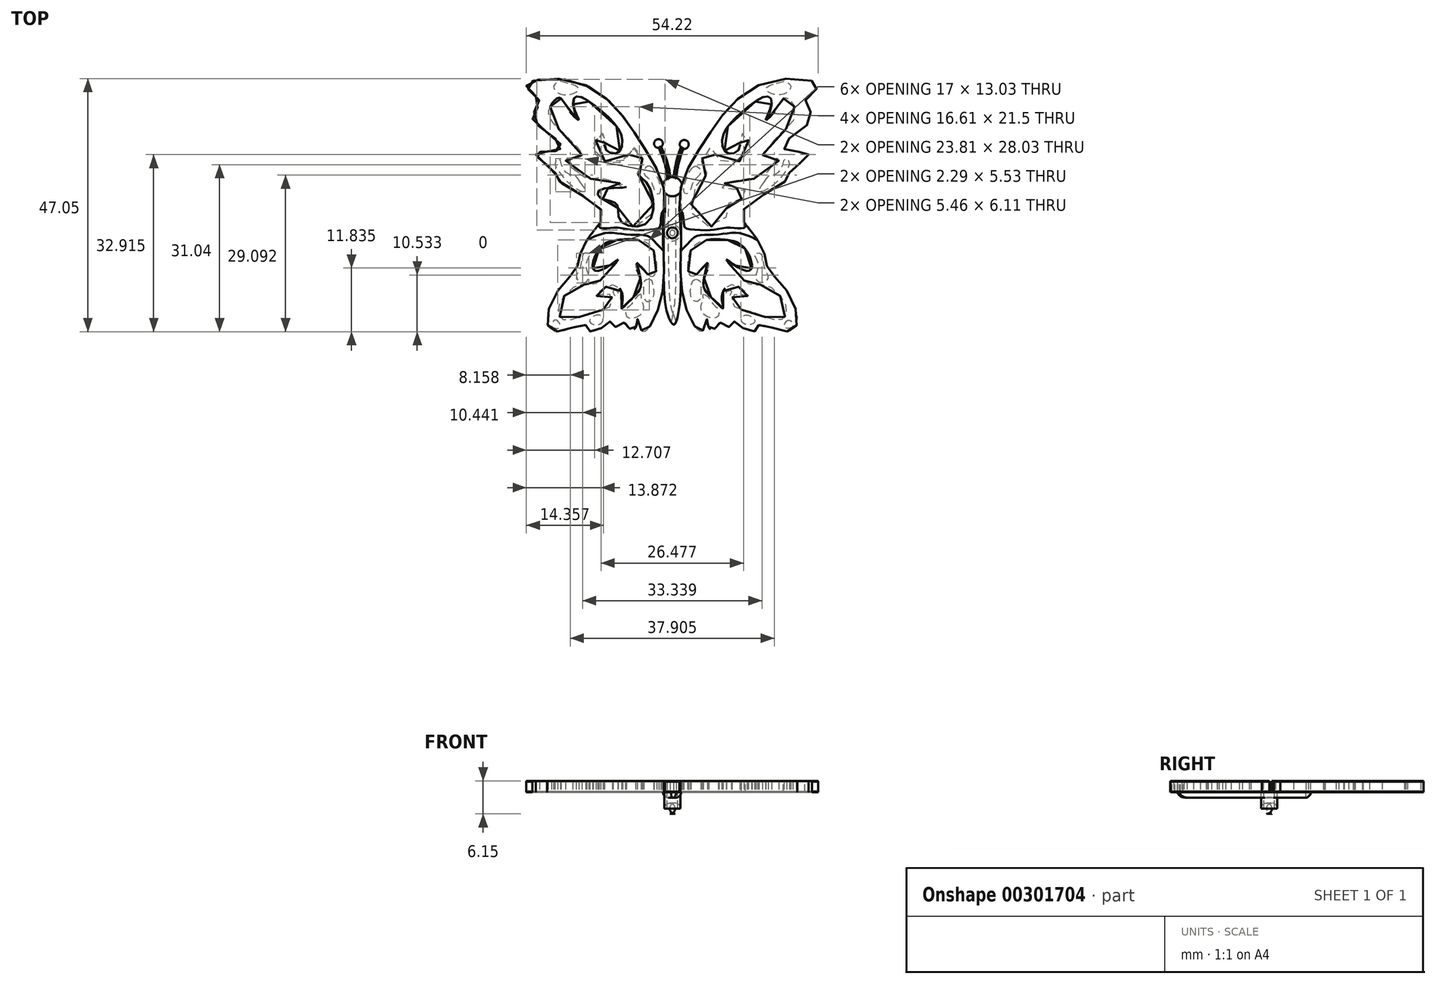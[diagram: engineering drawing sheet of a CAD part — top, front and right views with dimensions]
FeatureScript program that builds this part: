
annotation { "Feature Type Name" : "Feature", "Feature Type Description" : "" }
export const myFeature = defineFeature(function(context is Context, id is Id, definition is map)
    precondition{}
    {
        {
            var Q0;
            Q0=qCreatedBy(makeId("Top.planeOp"),FACE);
            var sketch = newSketch(context, id + "F0", { "sketchPlane" : qUnion([Q0])});
            skFitSpline(sketch, "E0", {"points": [v(3.62, 15.78) * mm, v(8.1, 22.3) * mm, v(17.17, 28.33) * mm, v(25.51, 27.33) * mm, v(23.06, 24.4) * mm, v(24.4, 21.43) * mm, v(19.29, 16.73) * mm, v(19.62, 15.33) * mm, v(23.6, 14.88) * mm, v(23.2, 13.8) * mm, v(20.17, 11.2) * mm, v(19.8, 10) * mm, v(11.56, 4.2) * mm, v(12.4, 1.11) * mm, v(15.39, -3.48) * mm, v(16.15, -6.56) * mm, v(19.7, -10.78) * mm, v(21.48, -17.24) * mm, v(18.78, -18.22) * mm, v(14.52, -17.12) * mm, v(13.9, -18.22) * mm, v(11.37, -17.59) * mm, v(9.8, -16.49) * mm, v(8.84, -17.52) * mm, v(7.16, -16.68) * mm, v(6.11, -18) * mm, v(5.16, -17.53) * mm, v(4.84, -16.03) * mm, v(4.01, -18.26) * mm, v(1.8, -16.04) * mm, v(0, -8.85) * mm, v(0, 0) * mm, v(0, 8.4) * mm, v(3.62, 15.78) * mm]});
            skFitSpline(sketch, "E1", {"points": [v(21.1, 23.42) * mm, v(21.2, 21.34) * mm, v(15.67, 15.5) * mm, v(15.5, 14) * mm, v(18.2, 13.66) * mm, v(14, 10.1) * mm, v(12.49, 10.25) * mm, v(6.95, 8.53) * mm, v(11.74, 8.05) * mm, v(12.11, 6.85) * mm, v(10.13, 5.96) * mm, v(8.56, 5.14) * mm, v(8.1, 2.24) * mm, v(2.94, 1.96) * mm, v(2.94, 8.98) * mm, v(4.9, 11.2) * mm, v(3.88, 13) * mm, v(5.47, 15.82) * mm, v(7.16, 13.57) * mm, v(11.21, 13.42) * mm, v(13.05, 16.2) * mm, v(11.08, 18.59) * mm, v(10.9, 15.8) * mm, v(8.56, 14.88) * mm, v(7.72, 17.69) * mm, v(10.9, 22.09) * mm, v(16.14, 25.37) * mm, v(16.8, 23.68) * mm, v(15.77, 20.97) * mm, v(17.69, 22.94) * mm, v(19.23, 25.09) * mm, v(20.17, 24.71) * mm, v(21.1, 23.42) * mm]});
            skFitSpline(sketch, "E2", {"points": [v(4.72, -1.32) * mm, v(8.84, -1.32) * mm, v(11.84, -2.82) * mm, v(13.16, -6.56) * mm, v(11.65, -6.94) * mm, v(8.47, -4.97) * mm, v(10.25, -7.22) * mm, v(13.16, -9.65) * mm, v(15.96, -9.75) * mm, v(19.62, -14.05) * mm, v(18.4, -16.2) * mm, v(13.16, -14.71) * mm, v(9.78, -13.5) * mm, v(10.06, -11.43) * mm, v(12.5, -11.71) * mm, v(12.12, -11.06) * mm, v(9.4, -9.65) * mm, v(7.62, -11.62) * mm, v(7.81, -14.06) * mm, v(6.31, -12.65) * mm, v(4.16, -9.47) * mm, v(5.19, -5.81) * mm, v(4.72, -5.63) * mm, v(3.03, -7.6) * mm, v(2, -8.06) * mm, v(1.35, -6.94) * mm, v(2, -3) * mm, v(4.72, -1.32) * mm]});
            skFitSpline(sketch, "E3", {"points": [v(17.73, 27.77) * mm, v(18.86, 28.09) * mm, v(19.76, 28.01) * mm, v(20.43, 27.23) * mm, v(19.87, 26.2) * mm, v(17.97, 25.65) * mm, v(16.23, 26.2) * mm, v(15.76, 26.8) * mm, v(16.86, 27.53) * mm, v(17.73, 27.77) * mm]});
            skFitSpline(sketch, "E4", {"points": [v(15.48, 9.43) * mm, v(16.48, 10.66) * mm, v(17.68, 10.96) * mm, v(18.85, 12.36) * mm, v(19.4, 13.8) * mm, v(20.17, 13.05) * mm, v(19.43, 11.38) * mm, v(18.32, 9.96) * mm, v(15.76, 7.93) * mm, v(14.5, 7.76) * mm, v(15.48, 9.43) * mm]});
            skFitSpline(sketch, "E5", {"points": [v(2.27, 12.22) * mm, v(2.94, 12.38) * mm, v(3.73, 11.27) * mm, v(2.43, 9.7) * mm, v(1.52, 7.5) * mm, v(0.81, 7.3) * mm, v(0.54, 8.36) * mm, v(1.52, 11.2) * mm, v(2.27, 12.22) * mm]});
            skFitSpline(sketch, "E6", {"points": [v(14.05, -3.77) * mm, v(14.84, -3.84) * mm, v(15.26, -5.17) * mm, v(15.7, -7.06) * mm, v(16.23, -8.1) * mm, v(15.6, -9.11) * mm, v(14.48, -9.18) * mm, v(13.93, -8.16) * mm, v(14.22, -7.04) * mm, v(14.4, -6.12) * mm, v(14.1, -4.92) * mm, v(13.7, -3.96) * mm, v(14.05, -3.77) * mm]});
            skFitSpline(sketch, "E7", {"points": [v(8.84, -10.78) * mm, v(9.35, -10.78) * mm, v(9.24, -11.43) * mm, v(8.84, -11.63) * mm, v(8.44, -11.12) * mm, v(8.84, -10.78) * mm]});
            skFitSpline(sketch, "E8", {"points": [v(2.43, -8.72) * mm, v(3.47, -8.85) * mm, v(3.73, -10) * mm, v(3.73, -11.43) * mm, v(3.31, -12.65) * mm, v(2.43, -12.65) * mm, v(1.8, -11.43) * mm, v(2, -9.47) * mm, v(2.43, -8.72) * mm]});
            skFitSpline(sketch, "E9", {"points": [v(4.16, -11.43) * mm, v(4.94, -11.82) * mm, v(6, -13.29) * mm, v(6.94, -14.25) * mm, v(6.9, -15.53) * mm, v(5.77, -15.85) * mm, v(4.16, -15.07) * mm, v(3.73, -13.53) * mm, v(4.16, -12.27) * mm, v(4.16, -11.43) * mm]});
            skFitSpline(sketch, "E10", {"points": [v(11.65, -15.43) * mm, v(13.07, -15.53) * mm, v(13.74, -16.49) * mm, v(12.7, -17.08) * mm, v(11.3, -16.49) * mm, v(11.65, -15.43) * mm]});
            skFitSpline(sketch, "E11", {"points": [v(19.4, -16.73) * mm, v(20.17, -16.23) * mm, v(20.82, -17.24) * mm, v(20.17, -17.72) * mm, v(19.23, -17.53) * mm, v(19.4, -16.73) * mm]});
            skFitSpline(sketch, "E12", {"points": [v(14.26, -1.36) * mm, v(12.63, -0.57) * mm, v(10.17, 0) * mm, v(6.28, -0.33) * mm, v(2.9, -0.61) * mm, v(1.57, -1.74) * mm, v(0, -3.4) * mm], "startDerivative": vector(-10.7, 6.1) * mm, "endDerivative": vector(-9.7, -12.04) * mm});
            skFitSpline(sketch, "E13", {"points": [v(11.7, 2.04) * mm, v(12, 1.28) * mm, v(11.81, 0.96) * mm, v(10.6, 0.84) * mm, v(9, 0.99) * mm, v(6.88, 0.7) * mm, v(4.9, 0.47) * mm, v(1.68, 0.66) * mm, v(0.68, 1.09) * mm, v(0.42, 3.4) * mm, v(-0.27, 4.56) * mm], "startDerivative": vector(6.08, -11.32) * mm, "endDerivative": vector(-8.37, 10.05) * mm});
            skSolve(sketch);
        }
        {
            var Q0;
            Q0=qCreatedBy(makeId("Top.planeOp"),FACE);
            var sketch = newSketch(context, id + "F1", { "sketchPlane" : qUnion([Q0])});
            skCircle(sketch, "E14", {"center": v(0.63, 16.43) * mm, "radius": 0.84 * mm});
            skCircle(sketch, "E15", {"center": v(-1.57, 8.6) * mm, "radius": 1.8 * mm});
            skFitSpline(sketch, "E16", {"points": [v(-1.33, 10.38) * mm, v(0, 15.89) * mm], "startDerivative": vector(0.59, 5.64) * mm, "endDerivative": vector(2.02, 4.96) * mm});
            skFitSpline(sketch, "E17", {"points": [v(-0.83, 10.24) * mm, v(0.45, 15.62) * mm], "startDerivative": vector(0.54, 5.8) * mm, "endDerivative": vector(2.53, 6.6) * mm});
            skCircle(sketch, "E18", {"center": v(-4.16, 16.6) * mm, "radius": 0.81 * mm});
            skFitSpline(sketch, "E19", {"points": [v(-3.65, 15.97) * mm, v(-2.01, 10.34) * mm], "startDerivative": vector(2.88, -5.93) * mm, "endDerivative": vector(0.23, -5.97) * mm});
            skFitSpline(sketch, "E20", {"points": [v(-4.1, 15.8) * mm, v(-2.54, 10.1) * mm], "startDerivative": vector(2.85, -7.12) * mm, "endDerivative": vector(0.3, -6.34) * mm});
            skFitSpline(sketch, "E21", {"points": [v(0, 7.7) * mm, v(0.03, 0) * mm, v(0, -9.31) * mm, v(-0.4, -14.6) * mm, v(-1.33, -17.08) * mm, v(-2.61, -14.6) * mm, v(-3.15, -9.6) * mm, v(-3.3, 0) * mm, v(-3.17, 7.78) * mm], "startDerivative": vector(0.94, -63.78) * mm, "endDerivative": vector(1.9, 50.03) * mm});
            skCircle(sketch, "E22", {"center": v(-1.57, 0) * mm, "radius": 1 * mm});
            skCircle(sketch, "E23", {"center": v(-1.57, 0) * mm, "radius": 1.5 * mm});
            skSolve(sketch);
        }
        {
            var Q0;
            Q0=qCreatedBy(makeId("Right.planeOp"),FACE);
            cPlane(context, id + "F2", {"entities" : qUnion([Q0]), "cplaneType" : CPlaneType.OFFSET, "offset" : 1.6 * mm, "oppositeDirection" : true, "width" : 150 * mm, "height" : 150 * mm});
        }
        {
            var Q0;
            Q0=makeQuery(id+"F0.imprint","IMPRINT",FACE,{"disambiguationData":[TD([[makeQuery(id+"F0.imprint","IMPRINT",EDGE,{"derivedFrom":sQuery(id+"F0.wireOp",EDGE,"E1")}),1.0]])]});
            var Q1;
            {var subQ0=sQuery(id+"F0.wireOp",EDGE,"E12");Q1=makeQuery(id+"F0.imprint","IMPRINT",FACE,{"disambiguationData":[TD([[makeQuery(id+"F0.imprint","IMPRINT",EDGE,{"derivedFrom":subQ0}),-1.0]])]});}
            var Q2;
            Q2=makeQuery(id+"F0.imprint","IMPRINT",FACE,{"disambiguationData":[TD([[makeQuery(id+"F0.imprint","IMPRINT",EDGE,{"derivedFrom":sQuery(id+"F0.wireOp",EDGE,"E2")}),1.0]])]});
            var Q3;
            Q3=makeQuery(id+"F0.imprint","IMPRINT",FACE,{"disambiguationData":[TD([[makeQuery(id+"F0.imprint","IMPRINT",EDGE,{"derivedFrom":sQuery(id+"F0.wireOp",EDGE,"E8")}),-1.0]])]});
            var Q4;
            Q4=makeQuery(id+"F0.imprint","IMPRINT",FACE,{"disambiguationData":[TD([[makeQuery(id+"F0.imprint","IMPRINT",EDGE,{"derivedFrom":sQuery(id+"F0.wireOp",EDGE,"E9")}),-1.0]])]});
            var Q5;
            Q5=makeQuery(id+"F0.imprint","IMPRINT",FACE,{"disambiguationData":[TD([[makeQuery(id+"F0.imprint","IMPRINT",EDGE,{"derivedFrom":sQuery(id+"F0.wireOp",EDGE,"E7")}),-1.0]])]});
            var Q6;
            Q6=makeQuery(id+"F0.imprint","IMPRINT",FACE,{"disambiguationData":[TD([[makeQuery(id+"F0.imprint","IMPRINT",EDGE,{"derivedFrom":sQuery(id+"F0.wireOp",EDGE,"E10")}),-1.0]])]});
            var Q7;
            Q7=makeQuery(id+"F0.imprint","IMPRINT",FACE,{"disambiguationData":[TD([[makeQuery(id+"F0.imprint","IMPRINT",EDGE,{"derivedFrom":sQuery(id+"F0.wireOp",EDGE,"E6")}),-1.0]])]});
            var Q8;
            Q8=makeQuery(id+"F0.imprint","IMPRINT",FACE,{"disambiguationData":[TD([[makeQuery(id+"F0.imprint","IMPRINT",EDGE,{"derivedFrom":sQuery(id+"F0.wireOp",EDGE,"E4")}),-1.0]])]});
            var Q9;
            Q9=makeQuery(id+"F0.imprint","IMPRINT",FACE,{"disambiguationData":[TD([[makeQuery(id+"F0.imprint","IMPRINT",EDGE,{"derivedFrom":sQuery(id+"F0.wireOp",EDGE,"E3")}),-1.0]])]});
            var Q10;
            Q10=makeQuery(id+"F0.imprint","IMPRINT",FACE,{"disambiguationData":[TD([[makeQuery(id+"F0.imprint","IMPRINT",EDGE,{"derivedFrom":sQuery(id+"F0.wireOp",EDGE,"E5")}),-1.0]])]});
            var Q11;
            Q11=makeQuery(id+"F0.imprint","IMPRINT",FACE,{"disambiguationData":[TD([[makeQuery(id+"F0.imprint","IMPRINT",EDGE,{"derivedFrom":sQuery(id+"F0.wireOp",EDGE,"E11")}),-1.0]])]});
            extrude(context, id + "F3", {"entities" : qUnion([Q0, Q1, Q2, Q3, Q4, Q5, Q6, Q7, Q8, Q9, Q10, Q11]), "depth" : 0.15 * mm});
        }
        {
            var Q0;
            Q0=makeQuery(id+"F0.imprint","IMPRINT",FACE,{"disambiguationData":[TD([[makeQuery(id+"F0.imprint","IMPRINT",EDGE,{"derivedFrom":sQuery(id+"F0.wireOp",EDGE,"E1")}),1.0]])]});
            var Q1;
            Q1=makeQuery(id+"F0.imprint","IMPRINT",FACE,{"disambiguationData":[TD([[makeQuery(id+"F0.imprint","IMPRINT",EDGE,{"derivedFrom":sQuery(id+"F0.wireOp",EDGE,"E2")}),1.0]])]});
            extrude(context, id + "F4", {"entities" : qUnion([Q0, Q1]), "depth" : 2 * mm});
        }
        {
            var Q0;
            Q0=makeQuery(id+"F3.opExtrude","SWEPT_BODY",BODY,{"disambiguationData":[OSD([sQuery(id+"F0.wireOp",EDGE,"E0"),sQuery(id+"F0.wireOp",EDGE,"E1"),sQuery(id+"F0.wireOp",EDGE,"E2")])]});
            transform(context, id + "F5", {"entities" : qUnion([Q0]), "transformType" : TransformType.TRANSLATION_3D, "dx" : 0 * mm, "dy" : 0 * mm, "dz" : 2 * mm, "makeCopy" : true});
        }
        {
            var Q0;
            {var subQ0=sQuery(id+"F0.wireOp",EDGE,"E12");Q0=makeQuery(id+"F0.imprint","IMPRINT",FACE,{"disambiguationData":[TD([[makeQuery(id+"F0.imprint","IMPRINT",EDGE,{"derivedFrom":subQ0}),-1.0]])]});}
            extrude(context, id + "F6", {"entities" : qUnion([Q0]), "depth" : 25 * mm});
        }
        {
            var Q0;
            Q0=makeQuery(id+"F6.opExtrude","SWEPT_BODY",BODY,{"disambiguationData":[OSD([sQuery(id+"F0.wireOp",EDGE,"E0"),sQuery(id+"F0.wireOp",EDGE,"E12"),sQuery(id+"F0.wireOp",EDGE,"E13")])]});
            var Q1;
            Q1=makeQuery(id+"F5.opPattern","COPY",BODY,{"derivedFrom":makeQuery(id+"F3.opExtrude","SWEPT_BODY",BODY,{"disambiguationData":[OSD([sQuery(id+"F0.wireOp",EDGE,"E0"),sQuery(id+"F0.wireOp",EDGE,"E1"),sQuery(id+"F0.wireOp",EDGE,"E2")])]}),"instanceName":"1"});
            booleanBodies(context, id + "F7", {"operationType" : BooleanOperationType.SUBTRACTION, "tools" : qUnion([Q0]), "targets" : qUnion([Q1])});
        }
        {
            var Q0;
            Q0=makeQuery(id+"F3.opExtrude","SWEPT_BODY",BODY,{"disambiguationData":[OSD([sQuery(id+"F0.wireOp",EDGE,"E0"),sQuery(id+"F0.wireOp",EDGE,"E1"),sQuery(id+"F0.wireOp",EDGE,"E2")])]});
            var Q1;
            Q1=makeQuery(id+"F4.opExtrude","SWEPT_BODY",BODY,{"disambiguationData":[OSD([sQuery(id+"F0.wireOp",EDGE,"E0"),sQuery(id+"F0.wireOp",EDGE,"E2"),sQuery(id+"F0.wireOp",EDGE,"E6"),sQuery(id+"F0.wireOp",EDGE,"E7"),sQuery(id+"F0.wireOp",EDGE,"E8"),sQuery(id+"F0.wireOp",EDGE,"E9"),sQuery(id+"F0.wireOp",EDGE,"E10"),sQuery(id+"F0.wireOp",EDGE,"E11"),sQuery(id+"F0.wireOp",EDGE,"E12")])]});
            var Q2;
            Q2=makeQuery(id+"F4.opExtrude","SWEPT_BODY",BODY,{"disambiguationData":[OSD([sQuery(id+"F0.wireOp",EDGE,"E0"),sQuery(id+"F0.wireOp",EDGE,"E1"),sQuery(id+"F0.wireOp",EDGE,"E3"),sQuery(id+"F0.wireOp",EDGE,"E4"),sQuery(id+"F0.wireOp",EDGE,"E5"),sQuery(id+"F0.wireOp",EDGE,"E13")])]});
            var Q3;
            Q3=makeQuery(id+"F7.opBoolean","SPLIT",BODY,{"disambiguationData":[OD(0.0)],"derivedFrom":makeQuery(id+"F5.opPattern","COPY",BODY,{"derivedFrom":makeQuery(id+"F3.opExtrude","SWEPT_BODY",BODY,{"disambiguationData":[OSD([sQuery(id+"F0.wireOp",EDGE,"E0"),sQuery(id+"F0.wireOp",EDGE,"E1"),sQuery(id+"F0.wireOp",EDGE,"E2")])]}),"instanceName":"1"})});
            var Q4;
            Q4=makeQuery(id+"F7.opBoolean","SPLIT",BODY,{"disambiguationData":[OD(1.0)],"derivedFrom":makeQuery(id+"F5.opPattern","COPY",BODY,{"derivedFrom":makeQuery(id+"F3.opExtrude","SWEPT_BODY",BODY,{"disambiguationData":[OSD([sQuery(id+"F0.wireOp",EDGE,"E0"),sQuery(id+"F0.wireOp",EDGE,"E1"),sQuery(id+"F0.wireOp",EDGE,"E2")])]}),"instanceName":"1"})});
            var Q5;
            Q5=qCreatedBy(id+"F2.planeOp",FACE);
            mirror(context, id + "F8", {"entities" : qUnion([Q0, Q1, Q2, Q3, Q4]), "mirrorPlane" : qUnion([Q5])});
        }
        {
            var Q0;
            {var subQ0=sQuery(id+"F1.wireOp",EDGE,"E21");Q0=makeQuery(id+"F1.imprint","IMPRINT",FACE,{"disambiguationData":[TD([[makeQuery(id+"F1.imprint","IMPRINT",EDGE,{"derivedFrom":subQ0}),-1.0]])]});}
            var Q1;
            Q1=makeQuery(id+"F1.imprint","IMPRINT",FACE,{"disambiguationData":[TD([[makeQuery(id+"F1.imprint","IMPRINT",EDGE,{"derivedFrom":sQuery(id+"F1.wireOp",EDGE,"E22")}),-1.0]])]});
            var Q2;
            Q2=makeQuery(id+"F1.imprint","IMPRINT",FACE,{"disambiguationData":[TD([[makeQuery(id+"F1.imprint","IMPRINT",EDGE,{"derivedFrom":sQuery(id+"F1.wireOp",EDGE,"E22")}),1.0]])]});
            var Q3;
            {var subQ0=sQuery(id+"F1.wireOp",EDGE,"E15");var subQ5=makeQuery(id+"F1.imprint","INTERSECT",VERTEX,{"derivedFrom":[subQ0,sQuery(id+"F1.wireOp",EDGE,"E16")]});Q3=makeQuery(id+"F1.imprint","IMPRINT",FACE,{"disambiguationData":[TD([[makeQuery(id+"F1.imprint","IMPRINT",EDGE,{"disambiguationData":[TD([[subQ5,1.0]])],"derivedFrom":subQ0}),1.0]])]});}
            var Q4;
            {var subQ0=sQuery(id+"F1.wireOp",EDGE,"E18");var subQ1=makeQuery(id+"F1.imprint","INTERSECT",VERTEX,{"derivedFrom":[subQ0,sQuery(id+"F1.wireOp",EDGE,"E19")]});Q4=makeQuery(id+"F1.imprint","IMPRINT",FACE,{"disambiguationData":[TD([[makeQuery(id+"F1.imprint","IMPRINT",EDGE,{"disambiguationData":[TD([[subQ1,1.0]])],"derivedFrom":subQ0}),1.0]])]});}
            var Q5;
            {var subQ0=sQuery(id+"F1.wireOp",EDGE,"E14");var subQ1=makeQuery(id+"F1.imprint","INTERSECT",VERTEX,{"derivedFrom":[subQ0,sQuery(id+"F1.wireOp",EDGE,"E16")]});Q5=makeQuery(id+"F1.imprint","IMPRINT",FACE,{"disambiguationData":[TD([[makeQuery(id+"F1.imprint","IMPRINT",EDGE,{"disambiguationData":[TD([[subQ1,-1.0]])],"derivedFrom":subQ0}),1.0]])]});}
            var Q6;
            {var subQ0=sQuery(id+"F1.wireOp",EDGE,"E16");Q6=makeQuery(id+"F1.imprint","IMPRINT",FACE,{"disambiguationData":[TD([[makeQuery(id+"F1.imprint","IMPRINT",EDGE,{"derivedFrom":subQ0}),-1.0]])]});}
            var Q7;
            {var subQ0=sQuery(id+"F1.wireOp",EDGE,"E19");Q7=makeQuery(id+"F1.imprint","IMPRINT",FACE,{"disambiguationData":[TD([[makeQuery(id+"F1.imprint","IMPRINT",EDGE,{"derivedFrom":subQ0}),-1.0]])]});}
            extrude(context, id + "F9", {"entities" : qUnion([Q0, Q1, Q2, Q3, Q4, Q5, Q6, Q7]), "depth" : 0.15 * mm});
        }
        {
            var Q0;
            {var subQ0=sQuery(id+"F1.wireOp",EDGE,"E15");var subQ5=makeQuery(id+"F1.imprint","INTERSECT",VERTEX,{"derivedFrom":[subQ0,sQuery(id+"F1.wireOp",EDGE,"E16")]});Q0=makeQuery(id+"F1.imprint","IMPRINT",FACE,{"disambiguationData":[TD([[makeQuery(id+"F1.imprint","IMPRINT",EDGE,{"disambiguationData":[TD([[subQ5,1.0]])],"derivedFrom":subQ0}),1.0]])]});}
            var Q1;
            {var subQ0=sQuery(id+"F1.wireOp",EDGE,"E18");var subQ1=makeQuery(id+"F1.imprint","INTERSECT",VERTEX,{"derivedFrom":[subQ0,sQuery(id+"F1.wireOp",EDGE,"E19")]});Q1=makeQuery(id+"F1.imprint","IMPRINT",FACE,{"disambiguationData":[TD([[makeQuery(id+"F1.imprint","IMPRINT",EDGE,{"disambiguationData":[TD([[subQ1,1.0]])],"derivedFrom":subQ0}),1.0]])]});}
            var Q2;
            {var subQ0=sQuery(id+"F1.wireOp",EDGE,"E14");var subQ1=makeQuery(id+"F1.imprint","INTERSECT",VERTEX,{"derivedFrom":[subQ0,sQuery(id+"F1.wireOp",EDGE,"E16")]});Q2=makeQuery(id+"F1.imprint","IMPRINT",FACE,{"disambiguationData":[TD([[makeQuery(id+"F1.imprint","IMPRINT",EDGE,{"disambiguationData":[TD([[subQ1,-1.0]])],"derivedFrom":subQ0}),1.0]])]});}
            var Q3;
            {var subQ0=sQuery(id+"F1.wireOp",EDGE,"E16");Q3=makeQuery(id+"F1.imprint","IMPRINT",FACE,{"disambiguationData":[TD([[makeQuery(id+"F1.imprint","IMPRINT",EDGE,{"derivedFrom":subQ0}),-1.0]])]});}
            var Q4;
            {var subQ0=sQuery(id+"F1.wireOp",EDGE,"E19");Q4=makeQuery(id+"F1.imprint","IMPRINT",FACE,{"disambiguationData":[TD([[makeQuery(id+"F1.imprint","IMPRINT",EDGE,{"derivedFrom":subQ0}),-1.0]])]});}
            extrude(context, id + "F10", {"entities" : qUnion([Q0, Q1, Q2, Q3, Q4]), "depth" : 2 * mm});
        }
        {
            var Q0;
            {var subQ0=sQuery(id+"F1.wireOp",EDGE,"E15");var subQ5=makeQuery(id+"F1.imprint","INTERSECT",VERTEX,{"derivedFrom":[subQ0,sQuery(id+"F1.wireOp",EDGE,"E16")]});Q0=makeQuery(id+"F1.imprint","IMPRINT",FACE,{"disambiguationData":[TD([[makeQuery(id+"F1.imprint","IMPRINT",EDGE,{"disambiguationData":[TD([[subQ5,1.0]])],"derivedFrom":subQ0}),1.0]])]});}
            var Q1;
            {var subQ0=sQuery(id+"F1.wireOp",EDGE,"E16");Q1=makeQuery(id+"F1.imprint","IMPRINT",FACE,{"disambiguationData":[TD([[makeQuery(id+"F1.imprint","IMPRINT",EDGE,{"derivedFrom":subQ0}),-1.0]])]});}
            var Q2;
            {var subQ0=sQuery(id+"F1.wireOp",EDGE,"E19");Q2=makeQuery(id+"F1.imprint","IMPRINT",FACE,{"disambiguationData":[TD([[makeQuery(id+"F1.imprint","IMPRINT",EDGE,{"derivedFrom":subQ0}),-1.0]])]});}
            var Q3;
            {var subQ0=sQuery(id+"F1.wireOp",EDGE,"E18");var subQ1=makeQuery(id+"F1.imprint","INTERSECT",VERTEX,{"derivedFrom":[subQ0,sQuery(id+"F1.wireOp",EDGE,"E19")]});Q3=makeQuery(id+"F1.imprint","IMPRINT",FACE,{"disambiguationData":[TD([[makeQuery(id+"F1.imprint","IMPRINT",EDGE,{"disambiguationData":[TD([[subQ1,1.0]])],"derivedFrom":subQ0}),1.0]])]});}
            var Q4;
            {var subQ0=sQuery(id+"F1.wireOp",EDGE,"E14");var subQ1=makeQuery(id+"F1.imprint","INTERSECT",VERTEX,{"derivedFrom":[subQ0,sQuery(id+"F1.wireOp",EDGE,"E16")]});Q4=makeQuery(id+"F1.imprint","IMPRINT",FACE,{"disambiguationData":[TD([[makeQuery(id+"F1.imprint","IMPRINT",EDGE,{"disambiguationData":[TD([[subQ1,-1.0]])],"derivedFrom":subQ0}),1.0]])]});}
            extrude(context, id + "F11", {"entities" : qUnion([Q0, Q1, Q2, Q3, Q4]), "depth" : 2.15 * mm});
        }
        {
            var Q0;
            Q0=makeQuery(id+"F11.opExtrude","CAP_EDGE",EDGE,{"disambiguationData":[OSD([sQuery(id+"F1.wireOp",EDGE,"E18")])],"isStart":false});
            var Q1;
            Q1=makeQuery(id+"F11.opExtrude","CAP_EDGE",EDGE,{"disambiguationData":[OSD([sQuery(id+"F1.wireOp",EDGE,"E19")])],"isStart":false});
            var Q2;
            Q2=makeQuery(id+"F11.opExtrude","CAP_EDGE",EDGE,{"disambiguationData":[OSD([sQuery(id+"F1.wireOp",EDGE,"E14")])],"isStart":false});
            var Q3;
            Q3=makeQuery(id+"F11.opExtrude","CAP_EDGE",EDGE,{"disambiguationData":[OSD([sQuery(id+"F1.wireOp",EDGE,"E16")])],"isStart":false});
            var Q4;
            Q4=makeQuery(id+"F11.opExtrude","CAP_EDGE",EDGE,{"disambiguationData":[OSD([sQuery(id+"F1.wireOp",EDGE,"E17")])],"isStart":false});
            var Q5;
            {var subQ0=sQuery(id+"F1.wireOp",EDGE,"E15");var subQ1=sQuery(id+"F1.wireOp",EDGE,"E21");var subQ2=makeQuery(id+"F1.imprint","INTERSECT",VERTEX,{"disambiguationData":[OD(0.0)],"derivedFrom":[subQ0,subQ1]});Q5=makeQuery(id+"F11.opExtrude","CAP_EDGE",EDGE,{"disambiguationData":[OSD([subQ0]),TDD([makeQuery(id+"F1.imprint","IMPRINT",EDGE,{"disambiguationData":[TD([[makeQuery(id+"F1.imprint","INTERSECT",VERTEX,{"derivedFrom":[subQ0,sQuery(id+"F1.wireOp",EDGE,"E20")]}),-1.0]])],"derivedFrom":subQ0}),makeQuery(id+"F1.imprint","IMPRINT",EDGE,{"disambiguationData":[TD([[subQ2,1.0]])],"derivedFrom":subQ0}),makeQuery(id+"F1.imprint","IMPRINT",EDGE,{"disambiguationData":[TD([[makeQuery(id+"F1.imprint","INTERSECT",VERTEX,{"derivedFrom":[subQ0,sQuery(id+"F1.wireOp",EDGE,"E17")]}),1.0]])],"derivedFrom":subQ0})])],"isStart":false});}
            var Q6;
            {var subQ0=sQuery(id+"F1.wireOp",EDGE,"E15");Q6=makeQuery(id+"F11.opExtrude","CAP_EDGE",EDGE,{"disambiguationData":[OSD([subQ0]),TDD([makeQuery(id+"F1.imprint","IMPRINT",EDGE,{"disambiguationData":[TD([[makeQuery(id+"F1.imprint","INTERSECT",VERTEX,{"derivedFrom":[subQ0,sQuery(id+"F1.wireOp",EDGE,"E16")]}),-1.0]])],"derivedFrom":subQ0})])],"isStart":false});}
            var Q7;
            Q7=makeQuery(id+"F11.opExtrude","CAP_EDGE",EDGE,{"disambiguationData":[OSD([sQuery(id+"F1.wireOp",EDGE,"E14")])],"isStart":true});
            var Q8;
            Q8=makeQuery(id+"F11.opExtrude","CAP_EDGE",EDGE,{"disambiguationData":[OSD([sQuery(id+"F1.wireOp",EDGE,"E16")])],"isStart":true});
            var Q9;
            Q9=makeQuery(id+"F11.opExtrude","CAP_EDGE",EDGE,{"disambiguationData":[OSD([sQuery(id+"F1.wireOp",EDGE,"E17")])],"isStart":true});
            var Q10;
            Q10=makeQuery(id+"F11.opExtrude","CAP_EDGE",EDGE,{"disambiguationData":[OSD([sQuery(id+"F1.wireOp",EDGE,"E19")])],"isStart":true});
            var Q11;
            Q11=makeQuery(id+"F11.opExtrude","CAP_EDGE",EDGE,{"disambiguationData":[OSD([sQuery(id+"F1.wireOp",EDGE,"E18")])],"isStart":true});
            var Q12;
            Q12=makeQuery(id+"F11.opExtrude","CAP_EDGE",EDGE,{"disambiguationData":[OSD([sQuery(id+"F1.wireOp",EDGE,"E20")])],"isStart":false});
            var Q13;
            Q13=makeQuery(id+"F11.opExtrude","CAP_EDGE",EDGE,{"disambiguationData":[OSD([sQuery(id+"F1.wireOp",EDGE,"E20")])],"isStart":true});
            var Q14;
            {var subQ0=sQuery(id+"F1.wireOp",EDGE,"E15");var subQ1=sQuery(id+"F1.wireOp",EDGE,"E21");var subQ2=makeQuery(id+"F1.imprint","INTERSECT",VERTEX,{"disambiguationData":[OD(0.0)],"derivedFrom":[subQ0,subQ1]});Q14=makeQuery(id+"F11.opExtrude","CAP_EDGE",EDGE,{"disambiguationData":[OSD([subQ0]),TDD([makeQuery(id+"F1.imprint","IMPRINT",EDGE,{"disambiguationData":[TD([[makeQuery(id+"F1.imprint","INTERSECT",VERTEX,{"derivedFrom":[subQ0,sQuery(id+"F1.wireOp",EDGE,"E20")]}),-1.0]])],"derivedFrom":subQ0}),makeQuery(id+"F1.imprint","IMPRINT",EDGE,{"disambiguationData":[TD([[subQ2,1.0]])],"derivedFrom":subQ0}),makeQuery(id+"F1.imprint","IMPRINT",EDGE,{"disambiguationData":[TD([[makeQuery(id+"F1.imprint","INTERSECT",VERTEX,{"derivedFrom":[subQ0,sQuery(id+"F1.wireOp",EDGE,"E17")]}),1.0]])],"derivedFrom":subQ0})])],"isStart":true});}
            var Q15;
            {var subQ0=sQuery(id+"F1.wireOp",EDGE,"E15");Q15=makeQuery(id+"F11.opExtrude","CAP_EDGE",EDGE,{"disambiguationData":[OSD([subQ0]),TDD([makeQuery(id+"F1.imprint","IMPRINT",EDGE,{"disambiguationData":[TD([[makeQuery(id+"F1.imprint","INTERSECT",VERTEX,{"derivedFrom":[subQ0,sQuery(id+"F1.wireOp",EDGE,"E16")]}),-1.0]])],"derivedFrom":subQ0})])],"isStart":true});}
            fillet(context, id + "F12", {"entities" : qUnion([Q0, Q1, Q2, Q3, Q4, Q5, Q6, Q7, Q8, Q9, Q10, Q11, Q12, Q13, Q14, Q15]), "radius" : 0.2 * mm, "tangentPropagation" : true, "allowEdgeOverflow" : false});
        }
        {
            var Q0;
            {var subQ0=sQuery(id+"F1.wireOp",EDGE,"E21");Q0=makeQuery(id+"F1.imprint","IMPRINT",FACE,{"disambiguationData":[TD([[makeQuery(id+"F1.imprint","IMPRINT",EDGE,{"derivedFrom":subQ0}),-1.0]])]});}
            var Q1;
            Q1=makeQuery(id+"F1.imprint","IMPRINT",FACE,{"disambiguationData":[TD([[makeQuery(id+"F1.imprint","IMPRINT",EDGE,{"derivedFrom":sQuery(id+"F1.wireOp",EDGE,"E22")}),-1.0]])]});
            var Q2;
            Q2=makeQuery(id+"F1.imprint","IMPRINT",FACE,{"disambiguationData":[TD([[makeQuery(id+"F1.imprint","IMPRINT",EDGE,{"derivedFrom":sQuery(id+"F1.wireOp",EDGE,"E22")}),1.0]])]});
            extrude(context, id + "F13", {"entities" : qUnion([Q0, Q1, Q2]), "oppositeDirection" : true, "depth" : 1 * mm});
        }
        {
            var Q0;
            Q0=makeQuery(id+"F1.imprint","IMPRINT",FACE,{"disambiguationData":[TD([[makeQuery(id+"F1.imprint","IMPRINT",EDGE,{"derivedFrom":sQuery(id+"F1.wireOp",EDGE,"E22")}),-1.0]])]});
            var Q1;
            Q1=makeQuery(id+"F1.imprint","IMPRINT",FACE,{"disambiguationData":[TD([[makeQuery(id+"F1.imprint","IMPRINT",EDGE,{"derivedFrom":sQuery(id+"F1.wireOp",EDGE,"E22")}),1.0]])]});
            extrude(context, id + "F14", {"entities" : qUnion([Q0, Q1]), "oppositeDirection" : true, "depth" : 4 * mm});
        }
        {
            var Q0;
            Q0=makeQuery(id+"F1.imprint","IMPRINT",FACE,{"disambiguationData":[TD([[makeQuery(id+"F1.imprint","IMPRINT",EDGE,{"derivedFrom":sQuery(id+"F1.wireOp",EDGE,"E22")}),1.0]])]});
            extrude(context, id + "F15", {"entities" : qUnion([Q0]), "operationType" : NewBodyOperationType.REMOVE, "oppositeDirection" : true, "depth" : 3 * mm});
        }
        {
            var Q0;
            Q0=makeQuery(id+"F1.imprint","IMPRINT",FACE,{"disambiguationData":[TD([[makeQuery(id+"F1.imprint","IMPRINT",EDGE,{"derivedFrom":sQuery(id+"F1.wireOp",EDGE,"E22")}),1.0]])]});
            extrude(context, id + "F16", {"entities" : qUnion([Q0]), "operationType" : NewBodyOperationType.REMOVE, "oppositeDirection" : true, "depth" : 3 * mm});
        }
        {
            var Q0;
            Q0=makeQuery(id+"F1.imprint","IMPRINT",FACE,{"disambiguationData":[TD([[makeQuery(id+"F1.imprint","IMPRINT",EDGE,{"derivedFrom":sQuery(id+"F1.wireOp",EDGE,"E22")}),1.0]])]});
            extrude(context, id + "F17", {"entities" : qUnion([Q0]), "operationType" : NewBodyOperationType.REMOVE, "depth" : 25 * mm});
        }
        {
            var Q0;
            Q0=makeQuery(id+"F13.opExtrude","CAP_EDGE",EDGE,{"disambiguationData":[OSD([sQuery(id+"F1.wireOp",EDGE,"E21")])],"isStart":false});
            var Q1;
            Q1=makeQuery(id+"F14.opExtrude","CAP_EDGE",EDGE,{"disambiguationData":[OSD([sQuery(id+"F1.wireOp",EDGE,"E23")])],"isStart":false});
            fillet(context, id + "F18", {"entities" : qUnion([Q0, Q1]), "radius" : 1 * mm, "tangentPropagation" : true, "allowEdgeOverflow" : false});
        }
        {
            var Q0;
            Q0=makeQuery(id+"F17.boolean.opBoolean","INTERSECT",EDGE,{"derivedFrom":[makeQuery(id+"F9.opExtrude","CAP_FACE",FACE,{"disambiguationData":[OSD([sQuery(id+"F1.wireOp",EDGE,"E14"),sQuery(id+"F1.wireOp",EDGE,"E15"),sQuery(id+"F1.wireOp",EDGE,"E16"),sQuery(id+"F1.wireOp",EDGE,"E17"),sQuery(id+"F1.wireOp",EDGE,"E18"),sQuery(id+"F1.wireOp",EDGE,"E19"),sQuery(id+"F1.wireOp",EDGE,"E20"),sQuery(id+"F1.wireOp",EDGE,"E21")])],"isStart":false}),makeQuery(id+"F17.opExtrude","SWEPT_FACE",FACE,{"disambiguationData":[OSD([sQuery(id+"F1.wireOp",EDGE,"E22")])]})]});
            fillet(context, id + "F19", {"entities" : qUnion([Q0]), "radius" : 0.5 * mm, "tangentPropagation" : true, "allowEdgeOverflow" : false});
        }
    });
